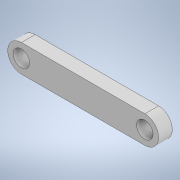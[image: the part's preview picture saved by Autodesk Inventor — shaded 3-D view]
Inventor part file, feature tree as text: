
AUTODESK INVENTOR PART (.ipt)
format: ipt  version: 2022 (Build 260153000, 153)  size: 105,984 bytes
history: native  units: mm
features: extrude x1, sketch x1
ambient origin geometry x8: Origin, YZ Plane, XZ Plane, XY Plane, X Axis, Y Axis, Z Axis, Center Point
bodies: Solid1 (feature_tree)
feature tree (2):
  extrude  "Extrusion1"  Depth=5.0mm
  sketch  "Sketch1"  dims[d0=10.0mm d1=6.0mm d3=45.0mm d4=5.0mm d5=0.0mm]
